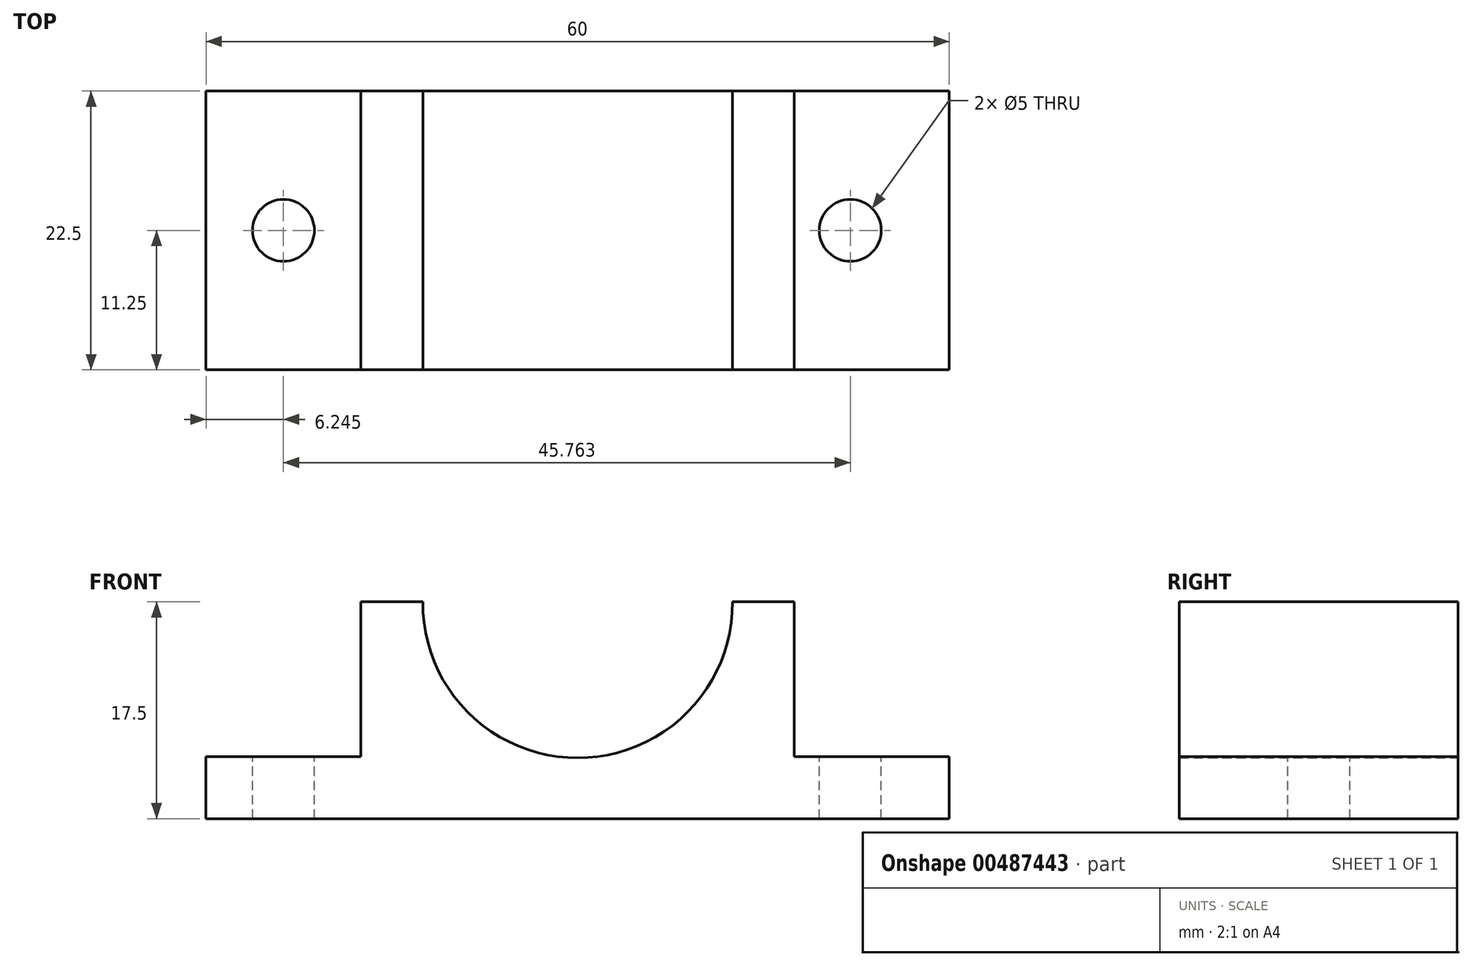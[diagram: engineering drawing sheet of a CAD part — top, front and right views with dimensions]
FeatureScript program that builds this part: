
annotation { "Feature Type Name" : "Feature", "Feature Type Description" : "" }
export const myFeature = defineFeature(function(context is Context, id is Id, definition is map)
    precondition{}
    {
        {
            var Q0;
            Q0=qCreatedBy(makeId("Front.planeOp"),FACE);
            var sketch = newSketch(context, id + "F0", { "sketchPlane" : qUnion([Q0])});
            skLineSegment(sketch, "E0", {"start": v(31.95, -5) * mm, "end": v(31.95, 0) * mm});
            skLineSegment(sketch, "E1", {"start": v(31.95, 0) * mm, "end": v(19.44, 0) * mm});
            skLineSegment(sketch, "E2", {"start": v(19.44, 0) * mm, "end": v(19.44, 12.5) * mm});
            skLineSegment(sketch, "E3", {"start": v(-15.55, 12.5) * mm, "end": v(-15.55, 0) * mm});
            skLineSegment(sketch, "E4", {"start": v(31.95, -5) * mm, "end": v(-28.05, -5) * mm});
            skLineSegment(sketch, "E5", {"start": v(-15.55, 12.5) * mm, "end": v(-10.55, 12.5) * mm});
            skLineSegment(sketch, "E6", {"start": v(14.44, 12.5) * mm, "end": v(19.44, 12.5) * mm});
            skArc(sketch, "E7", {"start": v(-10.55, 12.5) * mm, "mid": v(1.94, -0.1) * mm, "end": v(14.44, 12.5) * mm});
            skLineSegment(sketch, "E8", {"start": v(-28.05, -5) * mm, "end": v(-28.05, 0) * mm});
            skPoint(sketch, "E8.endSnap0", {"position": v(-18.33, 0) * mm});
            skLineSegment(sketch, "E9", {"start": v(-15.55, 0) * mm, "end": v(-28.05, 0) * mm});
            skSolve(sketch);
        }
        {
            var Q0;
            Q0=makeQuery(id+"F0.imprint","IMPRINT",FACE,{"disambiguationData":[TD([[makeQuery(id+"F0.imprint","IMPRINT",EDGE,{"derivedFrom":sQuery(id+"F0.wireOp",EDGE,"E0")}),1.0]])]});
            extrude(context, id + "F1", {"entities" : qUnion([Q0]), "depth" : 22.5 * mm});
        }
        {
            var Q0;
            Q0=makeQuery(id+"F1.opExtrude","SWEPT_FACE",FACE,{"disambiguationData":[OSD([sQuery(id+"F0.wireOp",EDGE,"E1")])]});
            var sketch = newSketch(context, id + "F2", { "sketchPlane" : qUnion([Q0])});
            skCircle(sketch, "E10", {"center": v(23.96, -11.25) * mm, "radius": 2.5 * mm});
            skSolve(sketch);
        }
        {
            var Q0;
            Q0=makeQuery(id+"F2.imprint","IMPRINT",FACE,{"disambiguationData":[TD([[makeQuery(id+"F2.imprint","IMPRINT",EDGE,{"derivedFrom":sQuery(id+"F2.wireOp",EDGE,"E10")}),1.0]])]});
            extrude(context, id + "F3", {"entities" : qUnion([Q0]), "operationType" : NewBodyOperationType.REMOVE, "endBound" : BoundingType.THROUGH_ALL, "oppositeDirection" : true, "depth" : 25 * mm});
        }
        {
            var Q0;
            Q0=makeQuery(id+"F1.opExtrude","SWEPT_FACE",FACE,{"disambiguationData":[OSD([sQuery(id+"F0.wireOp",EDGE,"E9")])]});
            var sketch = newSketch(context, id + "F4", { "sketchPlane" : qUnion([Q0])});
            skCircle(sketch, "E11", {"center": v(-21.8, -11.25) * mm, "radius": 2.5 * mm});
            skSolve(sketch);
        }
        {
            var Q0;
            Q0=makeQuery(id+"F4.imprint","IMPRINT",FACE,{"disambiguationData":[TD([[makeQuery(id+"F4.imprint","IMPRINT",EDGE,{"derivedFrom":sQuery(id+"F4.wireOp",EDGE,"E11")}),1.0]])]});
            extrude(context, id + "F5", {"entities" : qUnion([Q0]), "operationType" : NewBodyOperationType.REMOVE, "oppositeDirection" : true, "depth" : 25 * mm});
        }
    });
